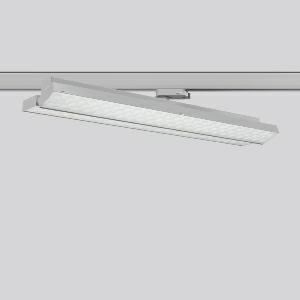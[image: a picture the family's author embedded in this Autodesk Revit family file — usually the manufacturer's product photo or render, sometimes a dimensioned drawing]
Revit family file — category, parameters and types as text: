
# Revit family: tx-move_742163_004_3_3268
name_source: partatom
category: Lighting Fixtures
units: mm (PartAtom-declared; Revit-internal decimal feet)

## family parameters
Cut with Voids When Loaded = No
Host = Face
Light Source = No
Part Type = Normal
Room Calculation Point = No
Round Connector Dimension = Use Diameter
Shared = No

## types (1)
- MultiLumen 1 (1 x LED Modul 835, 2875 lm, 3500)
    Apparent Load = 41 VA
    CIE Flux Codes = 65 90 98 100 100
    Color Rendering = 80
    Color Temperature = 3500
    Default Elevation = 1800 mm
    Description = Series: TX-MOVE
Multifunctional surface-mounted spotlight for area lighting. Very flat design. Housing: sheet steel, powder-coated. Rotation range: 356°. Swivel range: 90°. Consistent alignment possible with visible tilt scale. High-efficiency LED units with optimum light control thanks to clear plastic (PC) lens optics. Spezielle Mikrostrukturen reduzieren Gelbsaum. Asymmetrical light distribution. With multi adaptor for 3-circuit tracks 230 V. Suitable for Track on ceiling. MultiLumen: Luminous flux adjustable in 3 steps. Factory setting is the highest luminous flux. Environmentally friendly and resource-saving due to replaceable and recyclable components. 
Colour: silver, matt (approx. RAL 9006)
Length: 570 mm
Width: 119 mm
Height: 92 mm
Lamp: LED
Socket: without socket
Colour temperature: 3500K
Colour rendering index (CRI): 80
System power: 41 W
Rated luminous flux: 5750 lm
Luminous efficiency: 140 lm/W
System power 2: 57 W
Rated luminous flux 2: 7750 lm
Luminous efficiency 2: 136 lm/W
System power 3: 73 W
Rated luminous flux 3: 9450 lm
Luminous efficiency 3: 129 lm/W
Control gear: Regulated power supply
Protection class: I
Type of protection: IP 20
    Height = 75 mm
    Lamp = 1 x LED Modul 835
    Lamp Light Flux = 2875 lm
    Lamp count = 1
    Length = 569 mm
    Lifetime = 50000 h
    Luminous efficacy = 140 lm/W
    Manufacturer = RZB
    ModVariant = No
    Model = 742163.004.3
    Mounting Place = Ceiling
    Mounting Type = Rail mounted
    Number of Poles = 1
    OnlyDefault = Yes
    Power Factor = 1
    Product Name = TX-MOVE
    Product group = Track mounted projectors
    ProductGroupID = 301
    Protection Class = Protection class I
    Protection Degree = IP 20
    RLX_Detail_Level = 1
    RLX_Emergency_Light_Flux = 0 lm
    RLX_Emergency_Type = 0
    RLX_Emergency_Type_DB = No
    RlxData = <blob elided: 54053 chars, md5=eadba233>
    Socket = socket
    Standby Power = 0 W
    System Light Flux = 5750 lm
    System Power = 41 W
    Type Comments = MultiLumen 1
    Type Image = 742162.004.jpg
    URL = http://relux.com
    VarID = multilumen_1
    Voltage = 230 V
    Voltage Range = 220-240 V
    Weight = 0.00 kg
    Width = 119 mm

## geometry (parser evidence)
native form markers: Blend x4, Sweep x15
no freeform markers — native parametric forms only
